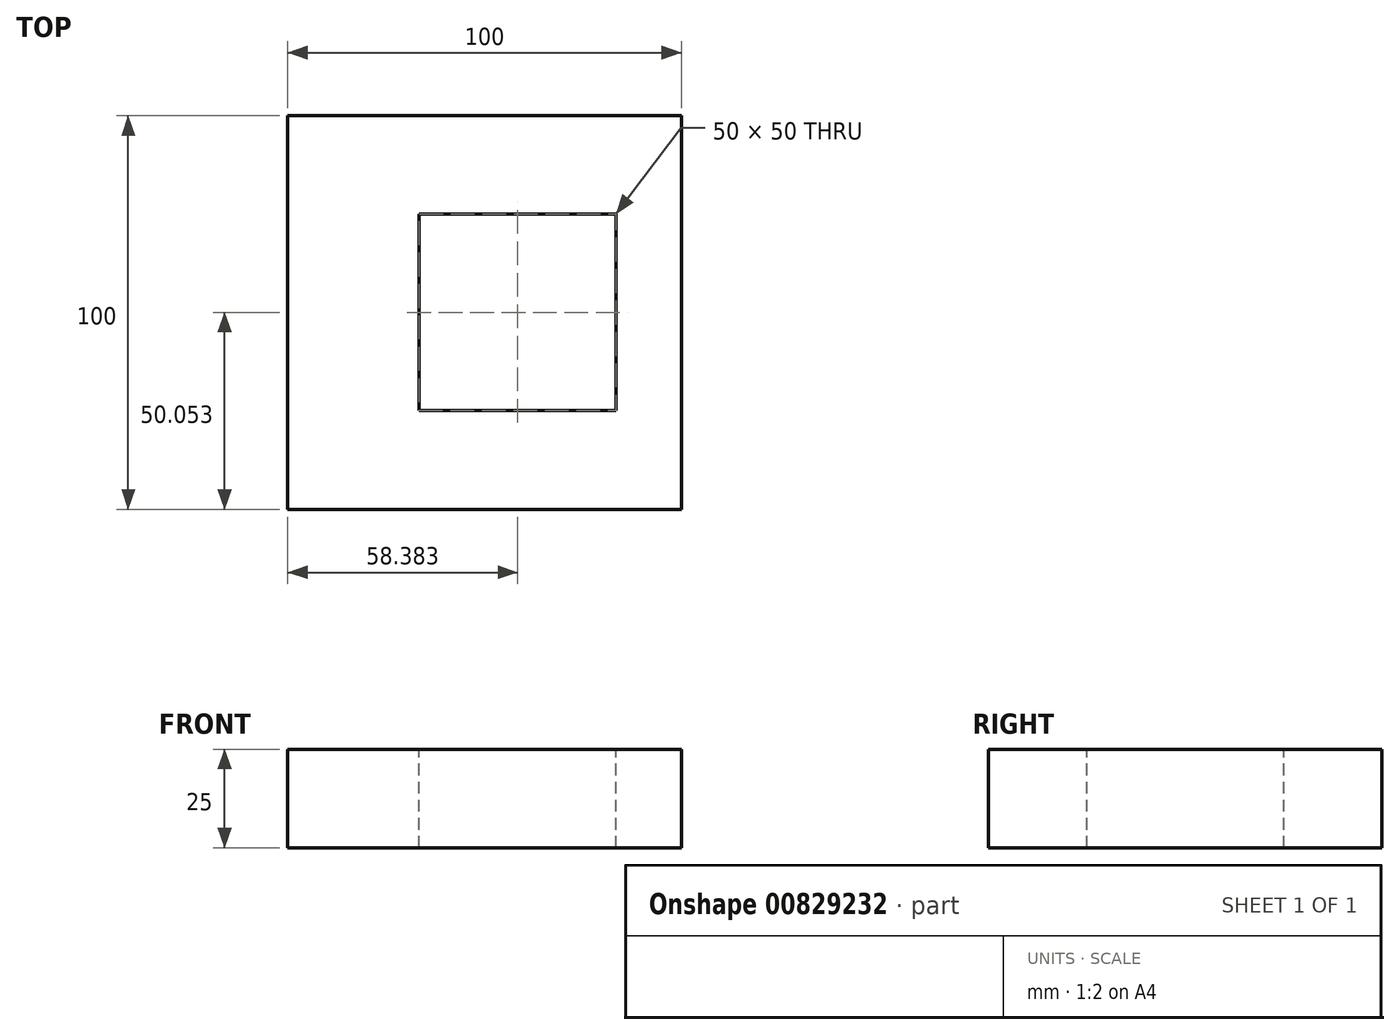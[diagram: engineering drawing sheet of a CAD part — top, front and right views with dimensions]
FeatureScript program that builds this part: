
annotation { "Feature Type Name" : "Feature", "Feature Type Description" : "" }
export const myFeature = defineFeature(function(context is Context, id is Id, definition is map)
    precondition{}
    {
        {
            var Q0;
            Q0=qCreatedBy(makeId("Top.planeOp"),FACE);
            var sketch = newSketch(context, id + "F0", { "sketchPlane" : qUnion([Q0])});
            skLineSegment(sketch, "E0.bottom", {"start": v(-60.3, 0) * mm, "end": v(39.7, 0) * mm});
            skLineSegment(sketch, "E0.top", {"start": v(-60.3, 100) * mm, "end": v(39.7, 100) * mm});
            skLineSegment(sketch, "E0.left", {"start": v(-60.3, 0) * mm, "end": v(-60.3, 100) * mm});
            skLineSegment(sketch, "E0.right", {"start": v(39.7, 0) * mm, "end": v(39.7, 100) * mm});
            skSolve(sketch);
        }
        {
            var Q0;
            Q0 = qSketchRegion(id + "F0", true);
            extrude(context, id + "F1", {"entities" : qUnion([Q0]), "depth" : 25 * mm, "offsetDistance" : 25 * mm});
        }
        {
            var Q0;
            Q0=makeQuery(id+"F1.opExtrude","CAP_FACE",FACE,{"disambiguationData":[OSD([sQuery(id+"F0.wireOp",EDGE,"E0.bottom"),sQuery(id+"F0.wireOp",EDGE,"E0.top"),sQuery(id+"F0.wireOp",EDGE,"E0.left"),sQuery(id+"F0.wireOp",EDGE,"E0.right")])],"isStart":false});
            var sketch = newSketch(context, id + "F2", { "sketchPlane" : qUnion([Q0])});
            skSolve(sketch);
        }
        {
            var Q0;
            Q0=makeQuery(id+"F2.imprint","IMPRINT",FACE,{"disambiguationData":[TD([[makeQuery(id+"F2.imprint","IMPRINT",EDGE,{"derivedFrom":makeQuery(id+"F1.opExtrude","CAP_EDGE",EDGE,{"disambiguationData":[OSD([sQuery(id+"F0.wireOp",EDGE,"E0.bottom")])],"isStart":false})}),1.0]])]});
            var sketch = newSketch(context, id + "F3", { "sketchPlane" : qUnion([Q0])});
            skLineSegment(sketch, "E1.bottom", {"start": v(-26.92, 75.05) * mm, "end": v(23.08, 75.05) * mm});
            skLineSegment(sketch, "E1.top", {"start": v(-26.92, 25.05) * mm, "end": v(23.08, 25.05) * mm});
            skLineSegment(sketch, "E1.left", {"start": v(-26.92, 75.05) * mm, "end": v(-26.92, 25.05) * mm});
            skLineSegment(sketch, "E1.right", {"start": v(23.08, 75.05) * mm, "end": v(23.08, 25.05) * mm});
            skSolve(sketch);
        }
        {
            var Q0;
            Q0 = qSketchRegion(id + "F3", true);
            extrude(context, id + "F4", {"entities" : qUnion([Q0]), "operationType" : NewBodyOperationType.REMOVE, "oppositeDirection" : true, "depth" : 25 * mm, "offsetDistance" : 25 * mm});
        }
    });
